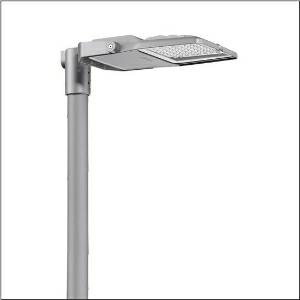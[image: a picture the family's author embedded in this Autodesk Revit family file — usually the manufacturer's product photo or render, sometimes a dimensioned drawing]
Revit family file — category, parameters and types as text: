
# Revit family: floodlight_fl_21_mini___pl61_5xa7776d4c3a_5b5f
name_source: partatom
category: Lighting Fixtures
units: mm (PartAtom-declared; Revit-internal decimal feet)

## family parameters
Cut with Voids When Loaded = No
Host = Face
Light Source = No
Part Type = Normal
Room Calculation Point = No
Round Connector Dimension = Use Diameter
Shared = No

## types (1)
- --- (1 x LED, 18260 lm, 142.9 W, 4000K)
    Apparent Load = 143 VA
    CIE Flux Codes = 33 65 98 100 100
    Color Rendering = 70
    Color Temperature = 4000K
    Default Elevation = 1800 mm
    Description = Floodlight FL 21 mini, floodlight, primary light control with lens, of PMMA, primary optical cover: protective disc, of toughened safety glass, transparent, light distribution: PL61, light emission: direct distribution, installation type: surface-mounted, LED, High Power LED, rated luminous flux: 18.260lm, luminous efficacy: 128lm/W, light colour: 740, colour temperature: 4000K, control gear: D4iSmart Interface (Zhaga), control: overheat protection, constant luminous flux control, time-dependent luminous flux control, flexible luminous flux parameterisation, pre-setting: logarithmic dimming characteristic, with terminal, 6-pole, mains connection: 220..240V, AC, 50/60Hz, start of lifetime: 143W, end of service life: 151W, reduction: 63W, mast bracket, of diecast aluminium, powder-coated, SITECO metallic grey (DB 702S), corrosivity category C5 mid according to DIN EN ISO 12944, suitable for swimming pools, chlorine-resistant, sealing non-destructively replaceable, mast bracket, of steel, galvanised, powder-coated, SITECO metallic grey (DB 702S), Smart Interface below and above, protection rating (complete): IP66, insulation class (complete): insulation class II (safety insulation), certification: CE, ENEC, VDE, protection symbol: D, impact resistance: IK08, permissible operating ambient temperature: -40..+40°C, permissible operating ambient temperature for outdoor applications: -40..+50°C, standard: DIN EN 12944, LABS conformity tested according to VDMA 24364:2018-05, packaging unit: 1 piece

Light Distribution: PL61
    Height = 70 mm
    Lamp = 1 x LED
    Lamp Light Flux = 18260 lm
    Lamp Power = 142.9 W
    Lamp count = 1
    Length = 485 mm
    Luminous efficacy = 128 lm/W
    Manufacturer = Siteco
    ModVariant = No
    Model = 5XA7776D4C3A
    Number of Poles = 1
    OnlyDefault = Yes
    Power Factor = 1
    Product Name = Floodlight FL 21 mini | PL61
    Product group = floodlight | pylon annexe
    ProductGroupID = 6201
    Protection Class = Protection class II
    Protection Degree = IP 66
    RLX_Detail_Level = 1
    RLX_Emergency_Light_Flux = 0 lm
    RLX_Emergency_Type = 0
    RLX_Emergency_Type_DB = No
    RlxData = <blob elided: 101313 chars, md5=6dfc767f>
    Socket = socket
    Standby Power = 0 W
    System Light Flux = 18260 lm
    System Power = 143 W
    Type Comments = factory setting: luminous flux: 100 % | dim-lin: 254 | 730 mA
    Type Image = l_1007125.jpg
    URL = http://relux.com
    VarID = @adj_102015
    Voltage = 0 V
    Weight = 0.00 kg
    Width = 337 mm

## geometry (parser evidence)
native form markers: Blend x4, Sweep x11
no freeform markers — native parametric forms only
